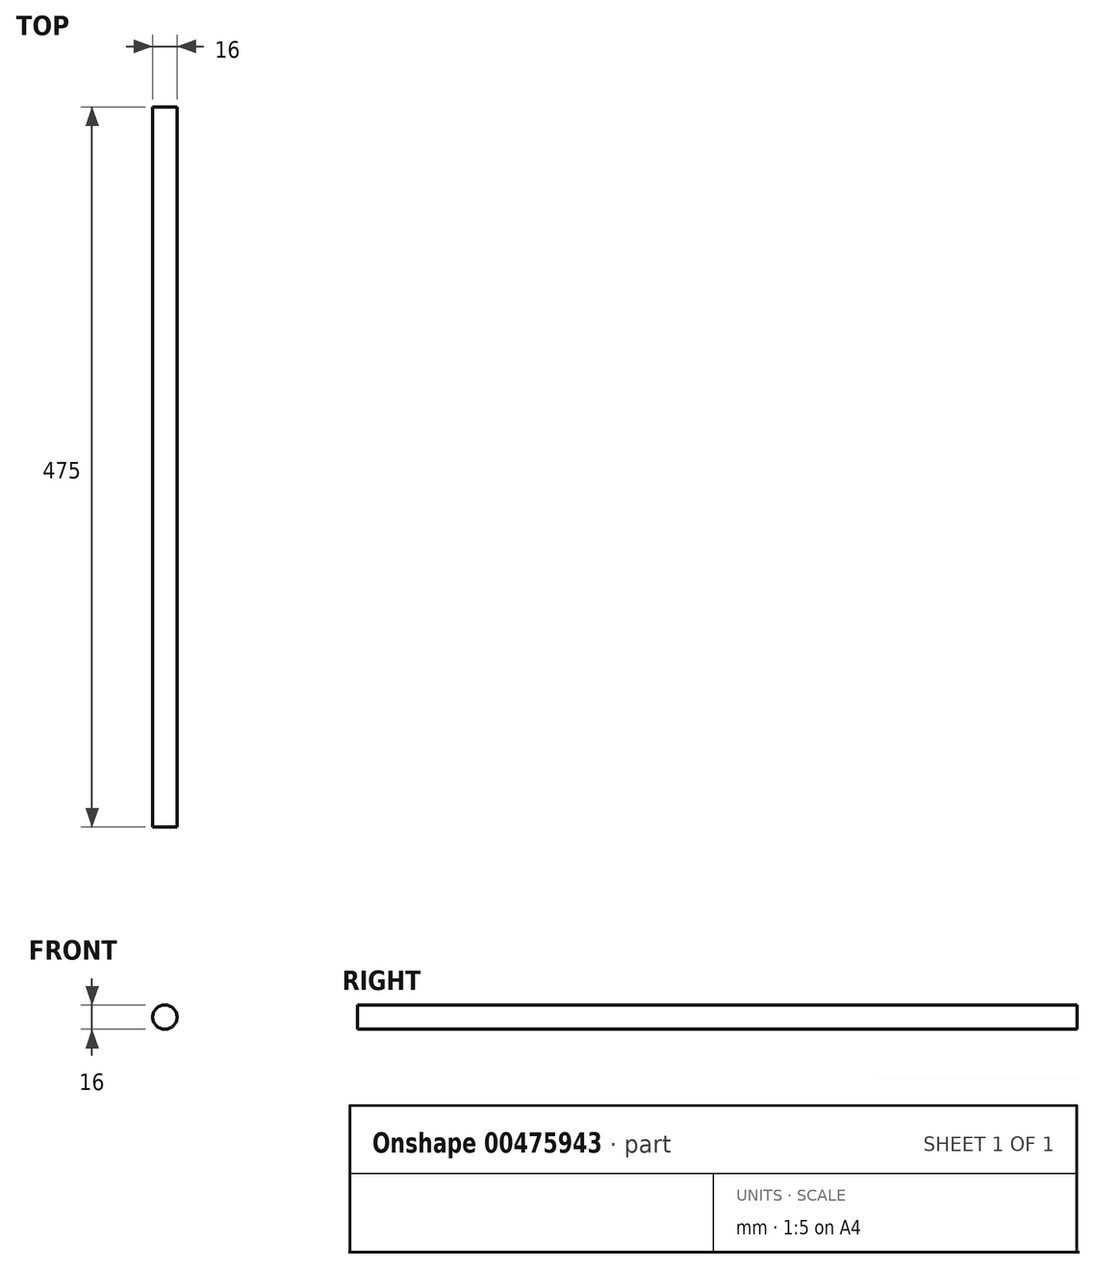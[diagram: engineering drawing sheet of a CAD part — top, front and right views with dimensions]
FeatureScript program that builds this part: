
annotation { "Feature Type Name" : "Feature", "Feature Type Description" : "" }
export const myFeature = defineFeature(function(context is Context, id is Id, definition is map)
    precondition{}
    {
        {
            var Q0;
            Q0=qCreatedBy(makeId("Front.planeOp"),FACE);
            var sketch = newSketch(context, id + "F0", { "sketchPlane" : qUnion([Q0])});
            skCircle(sketch, "E0", {"center": v(0, 0) * mm, "radius": 8 * mm});
            skSolve(sketch);
        }
        {
            var Q0;
            Q0 = qSketchRegion(id + "F0", true);
            extrude(context, id + "F1", {"entities" : qUnion([Q0]), "depth" : 500 * mm});
        }
        {
            var Q0;
            Q0=makeQuery(id+"F1.opExtrude","CAP_FACE",FACE,{"disambiguationData":[OSD([sQuery(id+"F0.wireOp",EDGE,"E0")])],"isStart":false});
            var sketch = newSketch(context, id + "F2", { "sketchPlane" : qUnion([Q0])});
            skCircle(sketch, "E1", {"center": v(0, 0) * mm, "radius": 5 * mm});
            skSolve(sketch);
        }
        {
            var Q0;
            Q0 = qSketchRegion(id + "F2", true);
            var Q1;
            Q1=makeQuery(id+"F2.imprint","IMPRINT",FACE,{"disambiguationData":[TD([[makeQuery(id+"F2.imprint","IMPRINT",EDGE,{"derivedFrom":sQuery(id+"F2.wireOp",EDGE,"E1")}),-1.0]])]});
            extrude(context, id + "F3", {"entities" : qUnion([Q0, Q1]), "operationType" : NewBodyOperationType.REMOVE, "oppositeDirection" : true, "depth" : 25 * mm});
        }
    });
